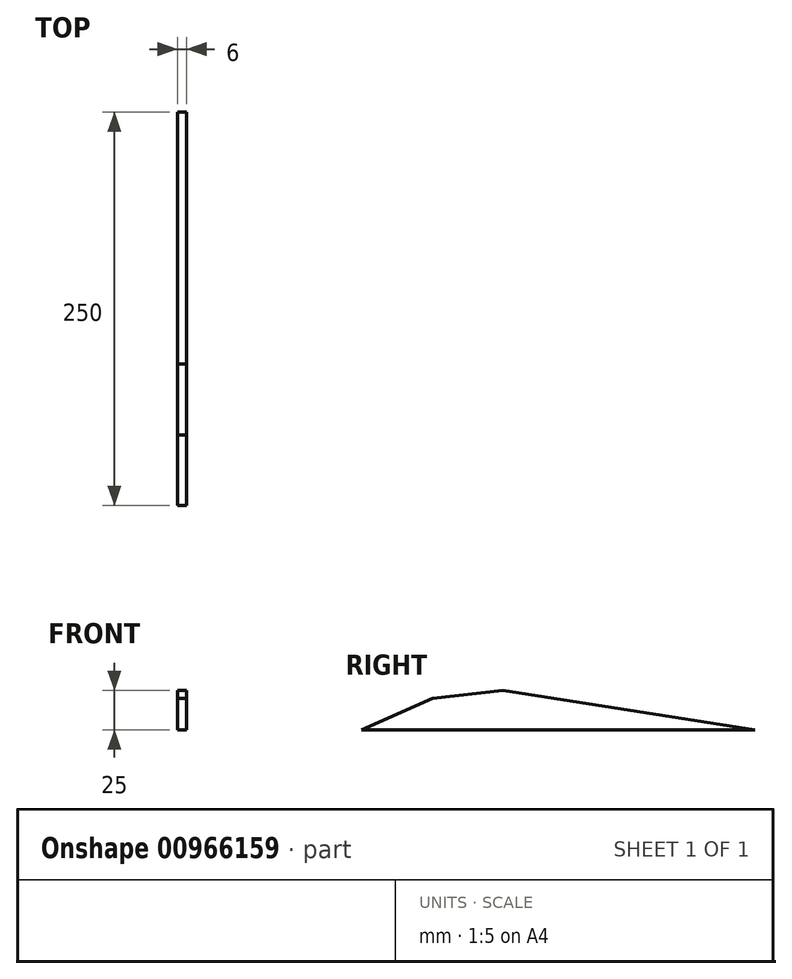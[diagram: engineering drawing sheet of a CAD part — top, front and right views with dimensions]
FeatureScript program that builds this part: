
annotation { "Feature Type Name" : "Feature", "Feature Type Description" : "" }
export const myFeature = defineFeature(function(context is Context, id is Id, definition is map)
    precondition{}
    {
        {
            var Q0;
            Q0=qCreatedBy(makeId("Right.planeOp"),FACE);
            var sketch = newSketch(context, id + "F0", { "sketchPlane" : qUnion([Q0])});
            skLineSegment(sketch, "E0", {"start": v(0, 0) * mm, "end": v(45, 20) * mm});
            skLineSegment(sketch, "E1", {"start": v(45, 20) * mm, "end": v(90, 25) * mm});
            skLineSegment(sketch, "E2", {"start": v(90, 25) * mm, "end": v(250, 0) * mm});
            skLineSegment(sketch, "E3", {"start": v(250, 0) * mm, "end": v(0, 0) * mm});
            skSolve(sketch);
        }
        {
            var Q0;
            Q0=makeQuery(id+"F0.imprint","IMPRINT",FACE,{"disambiguationData":[TD([[makeQuery(id+"F0.imprint","IMPRINT",EDGE,{"derivedFrom":sQuery(id+"F0.wireOp",EDGE,"E0")}),-1.0]])]});
            extrude(context, id + "F1", {"entities" : qUnion([Q0]), "endBound" : BoundingType.SYMMETRIC, "depth" : 6 * mm, "offsetDistance" : 25 * mm});
        }
    });
